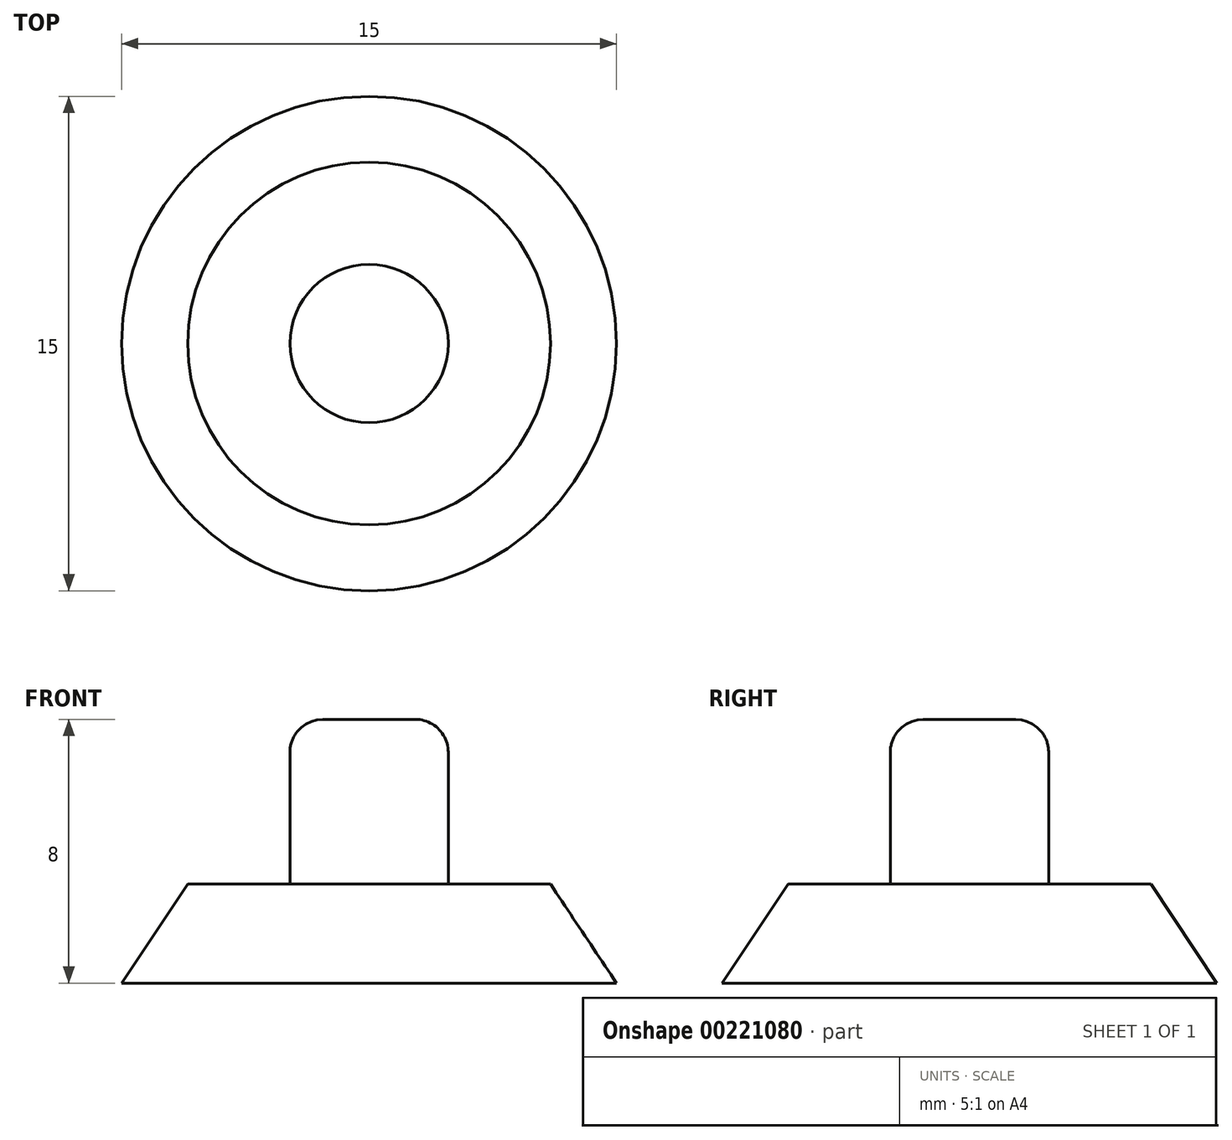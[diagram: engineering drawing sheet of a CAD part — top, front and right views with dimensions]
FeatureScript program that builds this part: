
annotation { "Feature Type Name" : "Feature", "Feature Type Description" : "" }
export const myFeature = defineFeature(function(context is Context, id is Id, definition is map)
    precondition{}
    {
        {
            var Q0;
            Q0=qCreatedBy(makeId("Top.planeOp"),FACE);
            var sketch = newSketch(context, id + "F0", { "sketchPlane" : qUnion([Q0])});
            skCircle(sketch, "E0", {"center": v(0, 0) * mm, "radius": 7.5 * mm});
            skSolve(sketch);
        }
        {
            var Q0;
            Q0=qSketchRegion(id+"F0",true);
            extrude(context, id + "F1", {"entities" : qUnion([Q0]), "depth" : 3 * mm});
        }
        {
            var Q0;
            Q0=makeQuery(id+"F1.opExtrude","CAP_EDGE",EDGE,{"disambiguationData":[OSD([sQuery(id+"F0.wireOp",EDGE,"E0")])],"isStart":false});
            chamfer(context, id + "F2", {"entities" : qUnion([Q0]), "chamferType" : ChamferType.TWO_OFFSETS, "width1" : 2 * mm, "oppositeDirection" : false, "width2" : 3 * mm});
        }
        {
            var Q0;
            Q0=makeQuery(id+"F1.opExtrude","CAP_FACE",FACE,{"disambiguationData":[OSD([sQuery(id+"F0.wireOp",EDGE,"E0")])],"isStart":false});
            var sketch = newSketch(context, id + "F3", { "sketchPlane" : qUnion([Q0])});
            skCircle(sketch, "E1", {"center": v(0, 0) * mm, "radius": 2.4 * mm});
            skCircle(sketch, "E2", {"center": v(0, 0) * mm, "radius": 6.04 * mm});
            skSolve(sketch);
        }
        {
            var Q0;
            Q0=makeQuery(id+"F3.imprint","IMPRINT",FACE,{"disambiguationData":[TD([[makeQuery(id+"F3.imprint","IMPRINT",EDGE,{"derivedFrom":sQuery(id+"F3.wireOp",EDGE,"E1")}),1.0]])]});
            extrude(context, id + "F4", {"entities" : qUnion([Q0]), "operationType" : NewBodyOperationType.ADD, "depth" : 5 * mm});
        }
        {
            var Q0;
            Q0=makeQuery(id+"F4.opExtrude","CAP_EDGE",EDGE,{"disambiguationData":[OSD([sQuery(id+"F3.wireOp",EDGE,"E1")])],"isStart":false});
            var Q1;
            Q1=makeQuery(id+"F4.opExtrude","CAP_EDGE",EDGE,{"disambiguationData":[OSD([sQuery(id+"F3.wireOp",EDGE,"E1")])],"isStart":true});
            fillet(context, id + "F5", {"entities" : qUnion([Q0, Q1]), "radius" : 1 * mm, "tangentPropagation" : true, "allowEdgeOverflow" : false});
        }
    });
